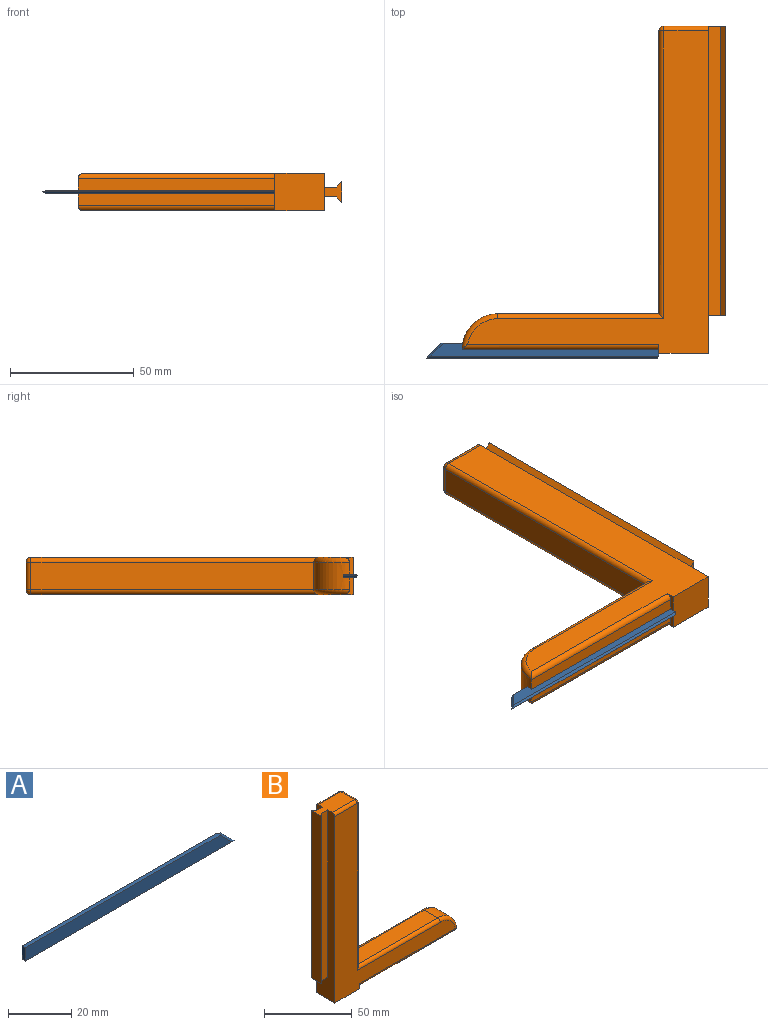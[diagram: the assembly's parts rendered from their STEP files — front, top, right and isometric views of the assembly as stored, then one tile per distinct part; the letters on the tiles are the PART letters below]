
ASSEMBLY  parts=2 mates=1
PART A: 9 faces, bbox 94x1.5x5.9 mm
  f0: plane 1.5x0.75mm, normal (-0.71,0,-0.71), area 0.8mm2, adj f1,f2,f5
  f1: plane 93.97x0.75mm, normal (0,-0.71,-0.71), area 98.3mm2, adj f0,f2,f3,f8
  f2: plane 93.97x0.75mm, normal (0,0.71,-0.71), area 98.3mm2, adj f0,f1,f4,f7
  f3: plane 92.16x5.18mm, normal (0,-1,0), area 463.8mm2, adj f1,f5,f6,f8
  f4: plane 92.16x5.18mm, normal (0,1,0), area 463.8mm2, adj f2,f5,f6,f7
  f5: plane 5.18x1.5mm, normal (-1,0,0), area 7.8mm2, adj f0,f3,f4,f6
  f6: plane 88.05x1.5mm, normal (0,0,1), area 131.3mm2, adj f3,f4,f5,f7,f8
  f7: plane 6.99x5.93mm, normal (0.5,0.71,0.5), area 8.3mm2, adj f2,f4,f6,f8
  f8: plane 6.99x5.93mm, normal (0.5,-0.71,0.5), area 8.3mm2, adj f1,f3,f6,f7
PART B: 33 faces, bbox 107.7x15x132 mm
  f0: plane 79.38x4.75mm, normal (0,0,-1), area 377.1mm2, adj f1,f18,f19,f22
  f1: plane 15x3.97mm, normal (1,0,0), area 27.5mm2, adj f0,f3,f4,f7,f14,f16,f17,f18
  f2: plane 132x15mm, normal (-1,0,0), area 1511.1mm2, adj f3,f4,f6,f7,f8,f9,f10,f28
  f3: plane 130x97.18mm, normal (0,1,0), area 3133.2mm2, adj f1,f2,f7,f20,f21,f22,f23,f32
  f4: plane 130x97.18mm, normal (0,-1,0), area 3133.2mm2, adj f1,f2,f7,f24,f25,f26,f27,f28
  f5: plane 114.15x11mm, normal (1,0,0), area 1255.6mm2, adj f15,f20,f24,f30
  f6: plane 25.08x11mm, normal (0,0,1), area 230.5mm2, adj f2,f8,f9,f11,f12,f13,f28,f30
  f7: plane 19.96x15mm, normal (0,0,-1), area 299.4mm2, adj f1,f2,f3,f4
  f8: plane 116.8x5mm, normal (0,-1,0), area 584mm2, adj f2,f6,f10,f13
  f9: plane 116.8x5mm, normal (0,1,0), area 584mm2, adj f2,f6,f10,f11
  f10: plane 8.24x7.12mm, normal (0,0,-1), area 33mm2, adj f2,f8,f9,f11,f12,f13
  f11: plane 116.8x2.12mm, normal (0.71,0.71,0), area 350.4mm2, adj f6,f9,f10,f12
  f12: plane 116.8x8.24mm, normal (-1,0,0), area 962.7mm2, adj f6,f10,f11,f13
  f13: plane 116.8x2.12mm, normal (0.71,-0.71,0), area 350.4mm2, adj f6,f8,f10,f12
  f14: plane 79.38x4.75mm, normal (0,0,-1), area 377.1mm2, adj f1,f17,f19,f25
  f15: plane 65x11mm, normal (0,0,1), area 715mm2, adj f5,f19,f21,f26
  f16: plane 79.17x1.5mm, normal (0,0,-1), area 118.7mm2, adj f1,f17,f18,f19
  f17: plane 79.38x2.5mm, normal (0,1,0), area 198.3mm2, adj f1,f14,f16,f19
  f18: plane 79.38x2.5mm, normal (0,-1,0), area 198.3mm2, adj f0,f1,f16,f19
  f19: cylinder r=14.38mm len=14.38mm, axis (0,-1,0), area 244.8mm2, adj f0,f14,f15,f16,f17,f18,f23,f27
  f20: cylinder r=2mm len=116.15mm, axis (0,0,-1), area 360.9mm2, adj f3,f5,f21,f31
  f21: cylinder r=2mm len=67mm, axis (1,0,0), area 206.5mm2, adj f3,f15,f20,f23
  f22: cylinder r=2mm len=79.38mm, axis (-1,0,0), area 247mm2, adj f0,f1,f3,f23
  f23: torus R=12.38mm, axis (0,1,0), area 65.1mm2, adj f3,f19,f21,f22
  f24: cylinder r=2mm len=116.15mm, axis (0,0,1), area 360.9mm2, adj f4,f5,f26,f29
  f25: cylinder r=2mm len=79.38mm, axis (1,0,0), area 247mm2, adj f1,f4,f14,f27
  f26: cylinder r=2mm len=67mm, axis (-1,0,0), area 206.5mm2, adj f4,f15,f24,f27
  f27: torus R=12.38mm, axis (0,1,0), area 65.1mm2, adj f4,f19,f25,f26
  f28: cylinder r=2mm len=17.96mm, axis (-1,0,0), area 56.4mm2, adj f2,f4,f6,f29
  f29: sphere r=2mm, area 6.3mm2, adj f24,f28,f30
  f30: cylinder r=2mm len=11mm, axis (0,-1,0), area 34.6mm2, adj f5,f6,f29,f31
  f31: sphere r=2mm, area 6.3mm2, adj f20,f30,f32
  f32: cylinder r=2mm len=17.96mm, axis (1,0,0), area 56.4mm2, adj f2,f3,f6,f31
PLACE A rot(axis=(0,-0.71,-0.71),180deg) t=(10.7,591.98,-268.13)mm
PLACE B rot(axis=(0,-0.71,-0.71),180deg) t=(30.68,602.43,-244.33)mm
MATE fastened A.f5 <-> B.f1  axis (1,0,0) through (20.7,606.4,-244.33)mm
